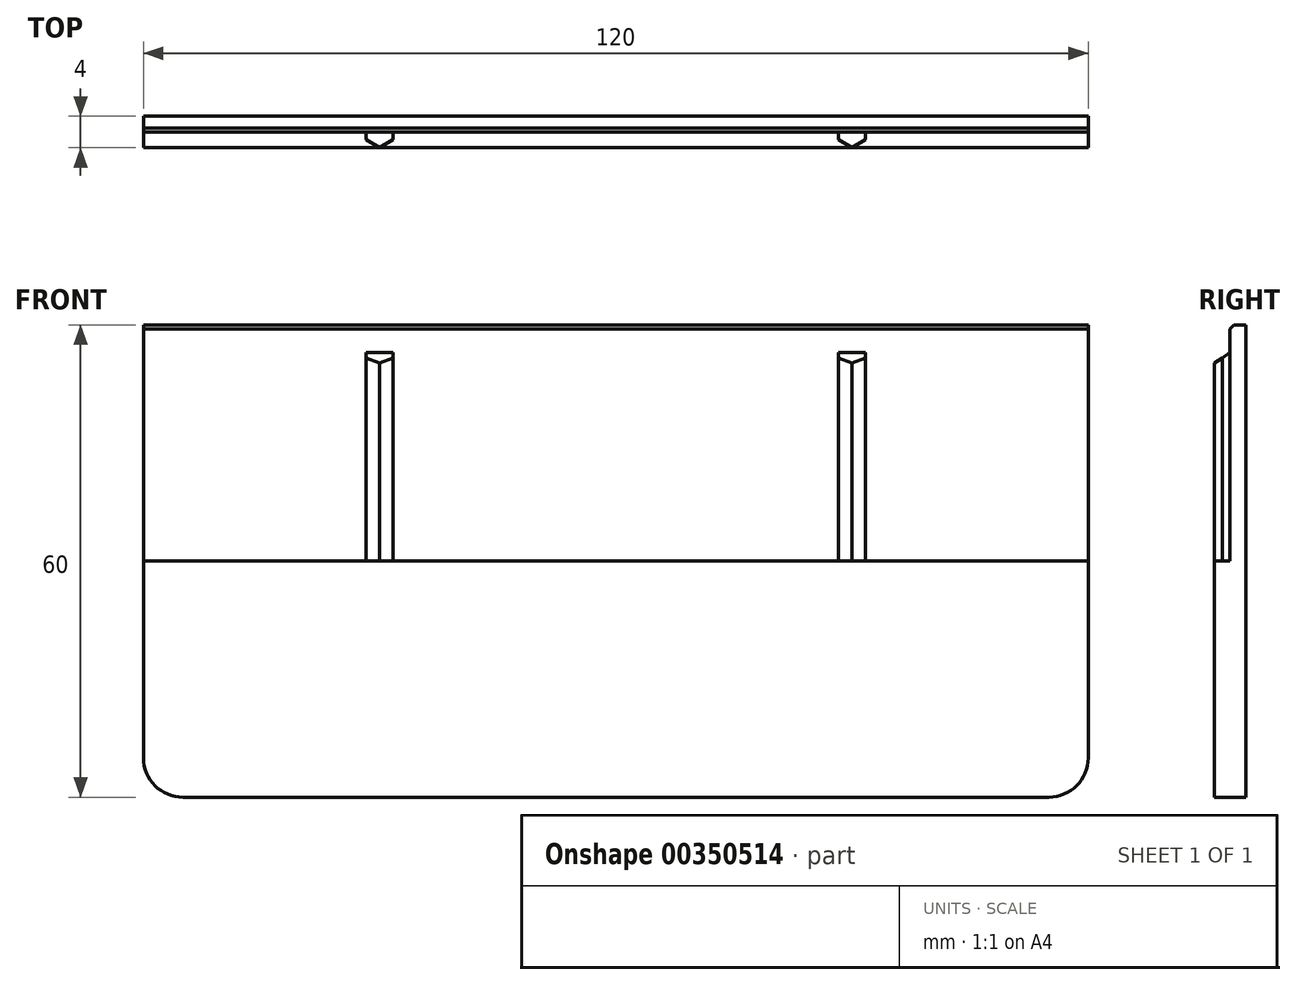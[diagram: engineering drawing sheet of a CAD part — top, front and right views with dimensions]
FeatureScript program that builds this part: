
annotation { "Feature Type Name" : "Feature", "Feature Type Description" : "" }
export const myFeature = defineFeature(function(context is Context, id is Id, definition is map)
    precondition{}
    {
        {
            var Q0;
            Q0=qCreatedBy(makeId("Front.planeOp"),FACE);
            var sketch = newSketch(context, id + "F0", { "sketchPlane" : qUnion([Q0])});
            skLineSegment(sketch, "E0.bottom", {"start": v(-60, 30) * mm, "end": v(60, 30) * mm, "construction": true});
            skLineSegment(sketch, "E0.top", {"start": v(-60, -30) * mm, "end": v(60, -30) * mm, "construction": true});
            skLineSegment(sketch, "E0.left", {"start": v(-60, 30) * mm, "end": v(-60, -30) * mm, "construction": true});
            skLineSegment(sketch, "E0.right", {"start": v(60, 30) * mm, "end": v(60, -30) * mm, "construction": true});
            skPoint(sketch, "E0.middle", {"position": v(0, 0) * mm});
            skLineSegment(sketch, "E1.bottom", {"start": v(-60, 30) * mm, "end": v(60, 30) * mm});
            skLineSegment(sketch, "E1.top", {"start": v(-60, -30) * mm, "end": v(60, -30) * mm});
            skLineSegment(sketch, "E1.left", {"start": v(-60, 30) * mm, "end": v(-60, -30) * mm});
            skLineSegment(sketch, "E1.right", {"start": v(60, 30) * mm, "end": v(60, -30) * mm});
            skLineSegment(sketch, "E2.bottom", {"start": v(-60, 0) * mm, "end": v(60, 0) * mm});
            skLineSegment(sketch, "E2.left", {"start": v(-60, 0) * mm, "end": v(-60, -30) * mm});
            skLineSegment(sketch, "E2.right", {"start": v(60, 0) * mm, "end": v(60, -30) * mm});
            skSolve(sketch);
        }
        {
            var Q0;
            Q0=makeQuery(id+"F0.imprint","IMPRINT",FACE,{"disambiguationData":[TD([[makeQuery(id+"F0.imprint","IMPRINT",EDGE,{"derivedFrom":sQuery(id+"F0.wireOp",EDGE,"E1.bottom")}),-1.0]])]});
            var Q1;
            Q1=makeQuery(id+"F0.imprint","IMPRINT",FACE,{"disambiguationData":[TD([[makeQuery(id+"F0.imprint","IMPRINT",EDGE,{"derivedFrom":sQuery(id+"F0.wireOp",EDGE,"E2.bottom")}),-1.0]])]});
            extrude(context, id + "F1", {"entities" : qUnion([Q0, Q1]), "depth" : 2 * mm});
        }
        {
            var Q0;
            Q0=makeQuery(id+"F1.opExtrude","CAP_FACE",FACE,{"disambiguationData":[OSD([sQuery(id+"F0.wireOp",EDGE,"E1.bottom"),sQuery(id+"F0.wireOp",EDGE,"E1.left"),sQuery(id+"F0.wireOp",EDGE,"E1.right"),sQuery(id+"F0.wireOp",EDGE,"E1.top"),sQuery(id+"F0.wireOp",EDGE,"E2.left"),sQuery(id+"F0.wireOp",EDGE,"E2.right")])],"isStart":false});
            var sketch = newSketch(context, id + "F2", { "sketchPlane" : qUnion([Q0])});
            skLineSegment(sketch, "E3.bottom", {"start": v(-60, -30) * mm, "end": v(60, -30) * mm});
            skLineSegment(sketch, "E3.top", {"start": v(-60, 0) * mm, "end": v(60, 0) * mm});
            skLineSegment(sketch, "E3.left", {"start": v(-60, -30) * mm, "end": v(-60, 0) * mm});
            skLineSegment(sketch, "E3.right", {"start": v(60, -30) * mm, "end": v(60, 0) * mm});
            skSolve(sketch);
        }
        {
            var Q0;
            Q0=makeQuery(id+"F2.imprint","IMPRINT",FACE,{"disambiguationData":[TD([[makeQuery(id+"F2.imprint","IMPRINT",EDGE,{"derivedFrom":sQuery(id+"F2.wireOp",EDGE,"E3.bottom")}),1.0]])]});
            extrude(context, id + "F3", {"entities" : qUnion([Q0]), "operationType" : NewBodyOperationType.ADD, "depth" : 2 * mm});
        }
        {
            var Q0;
            Q0=makeQuery(id+"F3.opExtrude","SWEPT_FACE",FACE,{"disambiguationData":[OSD([sQuery(id+"F2.wireOp",EDGE,"E3.top")])]});
            var sketch = newSketch(context, id + "F4", { "sketchPlane" : qUnion([Q0])});
            skLineSegment(sketch, "E4", {"start": v(-60, -2) * mm, "end": v(60, -2) * mm, "construction": true});
            skPoint(sketch, "E5", {"position": v(0, -2) * mm});
            skLineSegment(sketch, "E6", {"start": v(-60, -2) * mm, "end": v(0, -2) * mm});
            skCircle(sketch, "E7.cCircle", {"center": v(-30, -2) * mm, "radius": 1.7 * mm, "construction": true});
            skLineSegment(sketch, "E7.0", {"start": v(-31.7, -2.98) * mm, "end": v(-31.7, -1.02) * mm});
            skLineSegment(sketch, "E7.1", {"start": v(-31.7, -1.02) * mm, "end": v(-30, -0.04) * mm});
            skLineSegment(sketch, "E7.2", {"start": v(-30, -0.04) * mm, "end": v(-28.3, -1.02) * mm});
            skLineSegment(sketch, "E7.3", {"start": v(-28.3, -1.02) * mm, "end": v(-28.3, -2.98) * mm});
            skLineSegment(sketch, "E7.4", {"start": v(-28.3, -2.98) * mm, "end": v(-30, -3.96) * mm});
            skLineSegment(sketch, "E7.5", {"start": v(-30, -3.96) * mm, "end": v(-31.7, -2.98) * mm});
            skPoint(sketch, "E7.0.midPoint", {"position": v(-31.7, -2) * mm});
            skSolve(sketch);
        }
        {
            var Q0;
            {var subQ0=sQuery(id+"F4.wireOp",EDGE,"E7.4");Q0=makeQuery(id+"F4.imprint","IMPRINT",FACE,{"disambiguationData":[TD([[makeQuery(id+"F4.imprint","IMPRINT",EDGE,{"derivedFrom":subQ0}),-1.0]])]});}
            extrude(context, id + "F5", {"entities" : qUnion([Q0]), "operationType" : NewBodyOperationType.ADD, "depth" : 26.5 * mm});
        }
        {
            var Q0;
            Q0=makeQuery(id+"F3.opExtrude","SWEPT_FACE",FACE,{"disambiguationData":[OSD([sQuery(id+"F2.wireOp",EDGE,"E3.top")])]});
            var sketch = newSketch(context, id + "F6", { "sketchPlane" : qUnion([Q0])});
            skLineSegment(sketch, "E8", {"start": v(60, -2) * mm, "end": v(0, -2) * mm});
            skPoint(sketch, "E8.endSnap0", {"position": v(0, -4) * mm});
            skLineSegment(sketch, "E9", {"start": v(0, -2) * mm, "end": v(60, -2) * mm});
            skLineSegment(sketch, "E10", {"start": v(30, -2) * mm, "end": v(30, 0) * mm});
            skCircle(sketch, "E11.cCircle", {"center": v(30, -2) * mm, "radius": 1.7 * mm, "construction": true});
            skLineSegment(sketch, "E11.0", {"start": v(28.3, -2.98) * mm, "end": v(28.3, -1.02) * mm});
            skLineSegment(sketch, "E11.1", {"start": v(28.3, -1.02) * mm, "end": v(30, -0.04) * mm});
            skLineSegment(sketch, "E11.2", {"start": v(30, -0.04) * mm, "end": v(31.7, -1.02) * mm});
            skLineSegment(sketch, "E11.3", {"start": v(31.7, -1.02) * mm, "end": v(31.7, -2.98) * mm});
            skLineSegment(sketch, "E11.4", {"start": v(31.7, -2.98) * mm, "end": v(30, -3.96) * mm});
            skLineSegment(sketch, "E11.5", {"start": v(30, -3.96) * mm, "end": v(28.3, -2.98) * mm});
            skPoint(sketch, "E11.0.midPoint", {"position": v(28.3, -2) * mm});
            skSolve(sketch);
        }
        {
            var Q0;
            {var subQ0=sQuery(id+"F6.wireOp",EDGE,"E11.4");Q0=makeQuery(id+"F6.imprint","IMPRINT",FACE,{"disambiguationData":[TD([[makeQuery(id+"F6.imprint","IMPRINT",EDGE,{"derivedFrom":subQ0}),-1.0]])]});}
            extrude(context, id + "F7", {"entities" : qUnion([Q0]), "operationType" : NewBodyOperationType.ADD, "depth" : 26.5 * mm});
        }
        {
            var Q0;
            Q0=makeQuery(id+"F7.opExtrude","SWEPT_FACE",FACE,{"disambiguationData":[OSD([sQuery(id+"F6.wireOp",EDGE,"E11.3")])]});
            var sketch = newSketch(context, id + "F8", { "sketchPlane" : qUnion([Q0])});
            skLineSegment(sketch, "E12", {"start": v(-2, 26.5) * mm, "end": v(-3.97, 25.14) * mm});
            skLineSegment(sketch, "E13", {"start": v(-3.97, 25.14) * mm, "end": v(-4.77, 25.14) * mm});
            skLineSegment(sketch, "E14", {"start": v(-4.77, 25.14) * mm, "end": v(-4.77, 27.44) * mm});
            skLineSegment(sketch, "E15", {"start": v(-4.77, 27.44) * mm, "end": v(-2.98, 27.33) * mm});
            skLineSegment(sketch, "E16", {"start": v(-2.98, 27.33) * mm, "end": v(-2, 26.5) * mm});
            skSolve(sketch);
        }
        {
            var Q0;
            {var subQ0=sQuery(id+"F8.wireOp",EDGE,"E13");Q0=makeQuery(id+"F8.imprint","IMPRINT",FACE,{"disambiguationData":[TD([[makeQuery(id+"F8.imprint","IMPRINT",EDGE,{"derivedFrom":subQ0}),-1.0]])]});}
            var Q1;
            {var subQ1=sQuery(id+"F6.wireOp",EDGE,"E11.3");var subQ2=makeQuery(id+"F7.opExtrude","CAP_EDGE",EDGE,{"disambiguationData":[OSD([subQ1])],"isStart":false});Q1=makeQuery(id+"F8.imprint","IMPRINT",FACE,{"disambiguationData":[TD([[makeQuery(id+"F8.imprint","IMPRINT",EDGE,{"derivedFrom":subQ2}),1.0]])]});}
            extrude(context, id + "F9", {"entities" : qUnion([Q0, Q1]), "operationType" : NewBodyOperationType.REMOVE, "oppositeDirection" : true, "depth" : 83.2 * mm});
        }
        {
            var Q0;
            Q0=makeQuery(id+"F1.opExtrude","CAP_EDGE",EDGE,{"disambiguationData":[OSD([sQuery(id+"F0.wireOp",EDGE,"E1.bottom")])],"isStart":false});
            chamfer(context, id + "F10", {"entities" : qUnion([Q0]), "width" : 0.5 * mm, "tangentPropagation" : true});
        }
        {
            var Q0;
            Q0=makeQuery(id+"F3.boolean.opBoolean","MERGE",EDGE,{"derivedFrom":[makeQuery(id+"F1.opExtrude","SWEPT_EDGE",EDGE,{"disambiguationData":[OSD([sQuery(id+"F0.wireOp",EDGE,"E1.top"),sQuery(id+"F0.wireOp",EDGE,"E2.right")])]}),makeQuery(id+"F3.opExtrude","SWEPT_EDGE",EDGE,{"disambiguationData":[OSD([sQuery(id+"F2.wireOp",EDGE,"E3.bottom"),sQuery(id+"F2.wireOp",EDGE,"E3.right")])]})]});
            var Q1;
            Q1=makeQuery(id+"F3.boolean.opBoolean","MERGE",EDGE,{"derivedFrom":[makeQuery(id+"F1.opExtrude","SWEPT_EDGE",EDGE,{"disambiguationData":[OSD([sQuery(id+"F0.wireOp",EDGE,"E1.top"),sQuery(id+"F0.wireOp",EDGE,"E2.left")])]}),makeQuery(id+"F3.opExtrude","SWEPT_EDGE",EDGE,{"disambiguationData":[OSD([sQuery(id+"F2.wireOp",EDGE,"E3.bottom"),sQuery(id+"F2.wireOp",EDGE,"E3.left")])]})]});
            fillet(context, id + "F11", {"entities" : qUnion([Q0, Q1]), "radius" : 5 * mm, "tangentPropagation" : true, "allowEdgeOverflow" : false});
        }
    });
